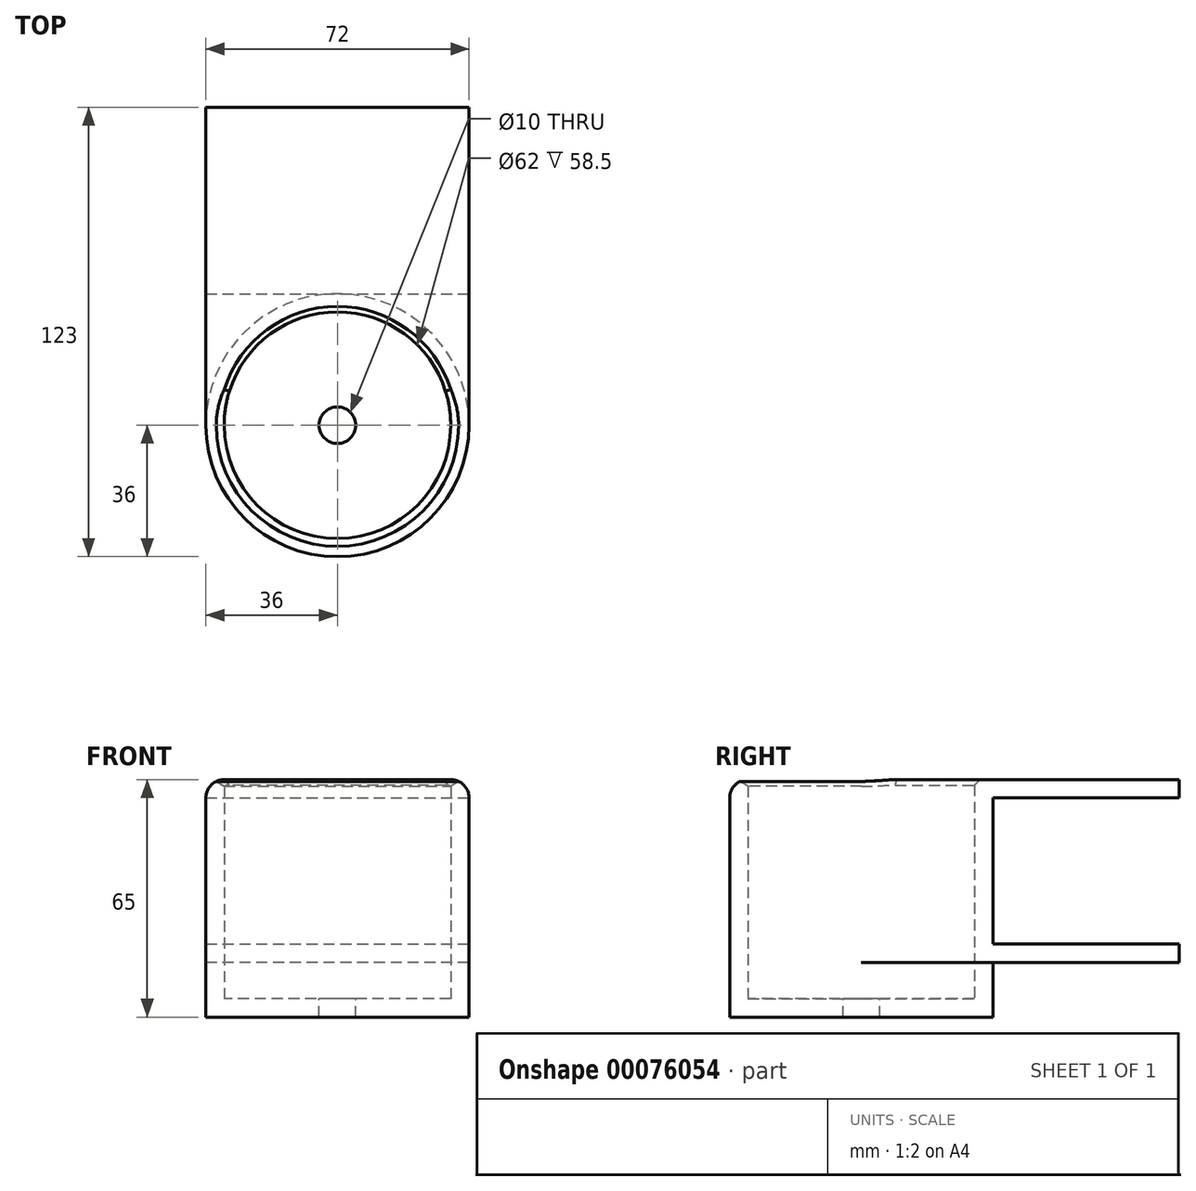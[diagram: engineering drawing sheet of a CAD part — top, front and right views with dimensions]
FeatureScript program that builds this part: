
annotation { "Feature Type Name" : "Feature", "Feature Type Description" : "" }
export const myFeature = defineFeature(function(context is Context, id is Id, definition is map)
    precondition{}
    {
        {
            var Q0;
            Q0=qCreatedBy(makeId("Top.planeOp"),FACE);
            var sketch = newSketch(context, id + "F0", { "sketchPlane" : qUnion([Q0])});
            skCircle(sketch, "E0", {"center": v(0, 0) * mm, "radius": 31 * mm});
            skCircle(sketch, "E1.0", {"center": v(0, 0) * mm, "radius": 36 * mm});
            skCircle(sketch, "E2", {"center": v(0, 0) * mm, "radius": 5 * mm});
            skSolve(sketch);
        }
        {
            var Q0;
            Q0 = qSketchRegion(id + "F0", true);
            var Q1;
            Q1=makeQuery(id+"F0.imprint","IMPRINT",FACE,{"disambiguationData":[TD([[makeQuery(id+"F0.imprint","IMPRINT",EDGE,{"derivedFrom":sQuery(id+"F0.wireOp",EDGE,"E0")}),1.0]])]});
            extrude(context, id + "F1", {"entities" : qUnion([Q0, Q1]), "oppositeDirection" : true, "depth" : 5 * mm});
        }
        {
            var Q0;
            Q0 = qSketchRegion(id + "F0", true);
            extrude(context, id + "F2", {"entities" : qUnion([Q0]), "operationType" : NewBodyOperationType.ADD, "depth" : 60 * mm});
        }
        {
            var Q0;
            Q0=makeQuery(id+"F2.opExtrude","CAP_FACE",FACE,{"disambiguationData":[OSD([sQuery(id+"F0.wireOp",EDGE,"E0"),sQuery(id+"F0.wireOp",EDGE,"E1.0")])],"isStart":false});
            var sketch = newSketch(context, id + "F3", { "sketchPlane" : qUnion([Q0])});
            skCircle(sketch, "E3.0", {"center": v(0, 0) * mm, "radius": 36 * mm});
            skLineSegment(sketch, "E4", {"start": v(36, 0) * mm, "end": v(36, 87) * mm});
            skLineSegment(sketch, "E5", {"start": v(36, 87) * mm, "end": v(-36, 87) * mm});
            skLineSegment(sketch, "E6", {"start": v(-36, 87) * mm, "end": v(-36, 0) * mm});
            skLineSegment(sketch, "E7.bottom", {"start": v(36, 36) * mm, "end": v(-36, 36) * mm});
            skLineSegment(sketch, "E7.top", {"start": v(36, 42) * mm, "end": v(-36, 42) * mm});
            skLineSegment(sketch, "E7.left", {"start": v(36, 36) * mm, "end": v(36, 42) * mm});
            skLineSegment(sketch, "E7.right", {"start": v(-36, 36) * mm, "end": v(-36, 42) * mm});
            skSolve(sketch);
        }
        {
            var Q0;
            {var subQ0=sQuery(id+"F3.wireOp",EDGE,"E6");var subQ1=sQuery(id+"F3.wireOp",EDGE,"E3.0");var subQ2=makeQuery(id+"F3.imprint","INTERSECT",VERTEX,{"derivedFrom":[subQ1,subQ0]});Q0=makeQuery(id+"F3.imprint","IMPRINT",FACE,{"disambiguationData":[TD([[makeQuery(id+"F3.imprint","IMPRINT",EDGE,{"disambiguationData":[TD([[subQ2,1.0]])],"derivedFrom":subQ1}),-1.0]])]});}
            var Q1;
            Q1=makeQuery(id+"F3.imprint","IMPRINT",FACE,{"disambiguationData":[TD([[makeQuery(id+"F3.imprint","IMPRINT",EDGE,{"derivedFrom":sQuery(id+"F3.wireOp",EDGE,"E7.top")}),1.0]])]});
            var Q2;
            {var subQ0=sQuery(id+"F3.wireOp",EDGE,"E5");Q2=makeQuery(id+"F3.imprint","IMPRINT",FACE,{"disambiguationData":[TD([[makeQuery(id+"F3.imprint","IMPRINT",EDGE,{"derivedFrom":subQ0}),1.0]])]});}
            var Q3;
            {var subQ0=sQuery(id+"F3.wireOp",EDGE,"E4");var subQ1=sQuery(id+"F3.wireOp",EDGE,"E3.0");var subQ2=makeQuery(id+"F3.imprint","INTERSECT",VERTEX,{"derivedFrom":[subQ1,subQ0]});Q3=makeQuery(id+"F3.imprint","IMPRINT",FACE,{"disambiguationData":[TD([[makeQuery(id+"F3.imprint","IMPRINT",EDGE,{"disambiguationData":[TD([[subQ2,-1.0]])],"derivedFrom":subQ1}),-1.0]])]});}
            extrude(context, id + "F4", {"entities" : qUnion([Q0, Q1, Q2, Q3]), "operationType" : NewBodyOperationType.ADD, "oppositeDirection" : true, "depth" : 50 * mm});
        }
        {
            var Q0;
            Q0=makeQuery(id+"F4.opExtrude","SWEPT_FACE",FACE,{"disambiguationData":[OSD([sQuery(id+"F3.wireOp",EDGE,"E4"),sQuery(id+"F3.wireOp",EDGE,"E7.left")])]});
            var sketch = newSketch(context, id + "F5", { "sketchPlane" : qUnion([Q0])});
            skLineSegment(sketch, "E8", {"start": v(36, 10) * mm, "end": v(36, -5) * mm});
            skLineSegment(sketch, "E9", {"start": v(87, 55) * mm, "end": v(36, 55) * mm});
            skPoint(sketch, "E9.endSnap0", {"position": v(36, 2.5) * mm});
            skLineSegment(sketch, "E10", {"start": v(36, 55) * mm, "end": v(36, 15) * mm});
            skLineSegment(sketch, "E11", {"start": v(36, 15) * mm, "end": v(87, 15) * mm});
            skSolve(sketch);
        }
        {
            var Q0;
            {var subQ0=sQuery(id+"F5.wireOp",EDGE,"E9");Q0=makeQuery(id+"F5.imprint","IMPRINT",FACE,{"disambiguationData":[TD([[makeQuery(id+"F5.imprint","IMPRINT",EDGE,{"derivedFrom":subQ0}),1.0]])]});}
            extrude(context, id + "F6", {"entities" : qUnion([Q0]), "operationType" : NewBodyOperationType.REMOVE, "endBound" : BoundingType.THROUGH_ALL, "oppositeDirection" : true, "depth" : 25 * mm});
        }
        {
            var Q0;
            Q0=makeQuery(id+"F4.opExtrude","CAP_EDGE",EDGE,{"disambiguationData":[OSD([sQuery(id+"F3.wireOp",EDGE,"E4"),sQuery(id+"F3.wireOp",EDGE,"E7.left")])],"isStart":true});
            var Q1;
            Q1=makeQuery(id+"F2.opExtrude","CAP_EDGE",EDGE,{"disambiguationData":[OSD([sQuery(id+"F0.wireOp",EDGE,"E1.0")])],"isStart":false});
            var Q2;
            Q2=makeQuery(id+"F4.opExtrude","CAP_EDGE",EDGE,{"disambiguationData":[OSD([sQuery(id+"F3.wireOp",EDGE,"E6"),sQuery(id+"F3.wireOp",EDGE,"E7.right")])],"isStart":true});
            fillet(context, id + "F7", {"entities" : qUnion([Q0, Q1, Q2]), "radius" : 5 * mm, "tangentPropagation" : true, "allowEdgeOverflow" : false});
        }
        {
            var Q0;
            Q0=makeQuery(id+"F2.opExtrude","CAP_EDGE",EDGE,{"disambiguationData":[OSD([sQuery(id+"F0.wireOp",EDGE,"E0")])],"isStart":false});
            var Q1;
            Q1=makeQuery(id+"F7.opFillet","BLEND_EDGE",EDGE,{"blendedFrom":[makeQuery(id+"F2.opExtrude","CAP_EDGE",EDGE,{"disambiguationData":[OSD([sQuery(id+"F0.wireOp",EDGE,"E1.0")])],"isStart":false}),makeQuery(id+"F2.opExtrude","SWEPT_FACE",FACE,{"disambiguationData":[OSD([sQuery(id+"F0.wireOp",EDGE,"E0")])]})],"blendedInto":[makeQuery(id+"F2.opExtrude","SWEPT_FACE",FACE,{"disambiguationData":[OSD([sQuery(id+"F0.wireOp",EDGE,"E0")])]})]});
            chamfer(context, id + "F8", {"entities" : qUnion([Q0, Q1]), "width" : 1.5 * mm, "tangentPropagation" : true});
        }
    });
